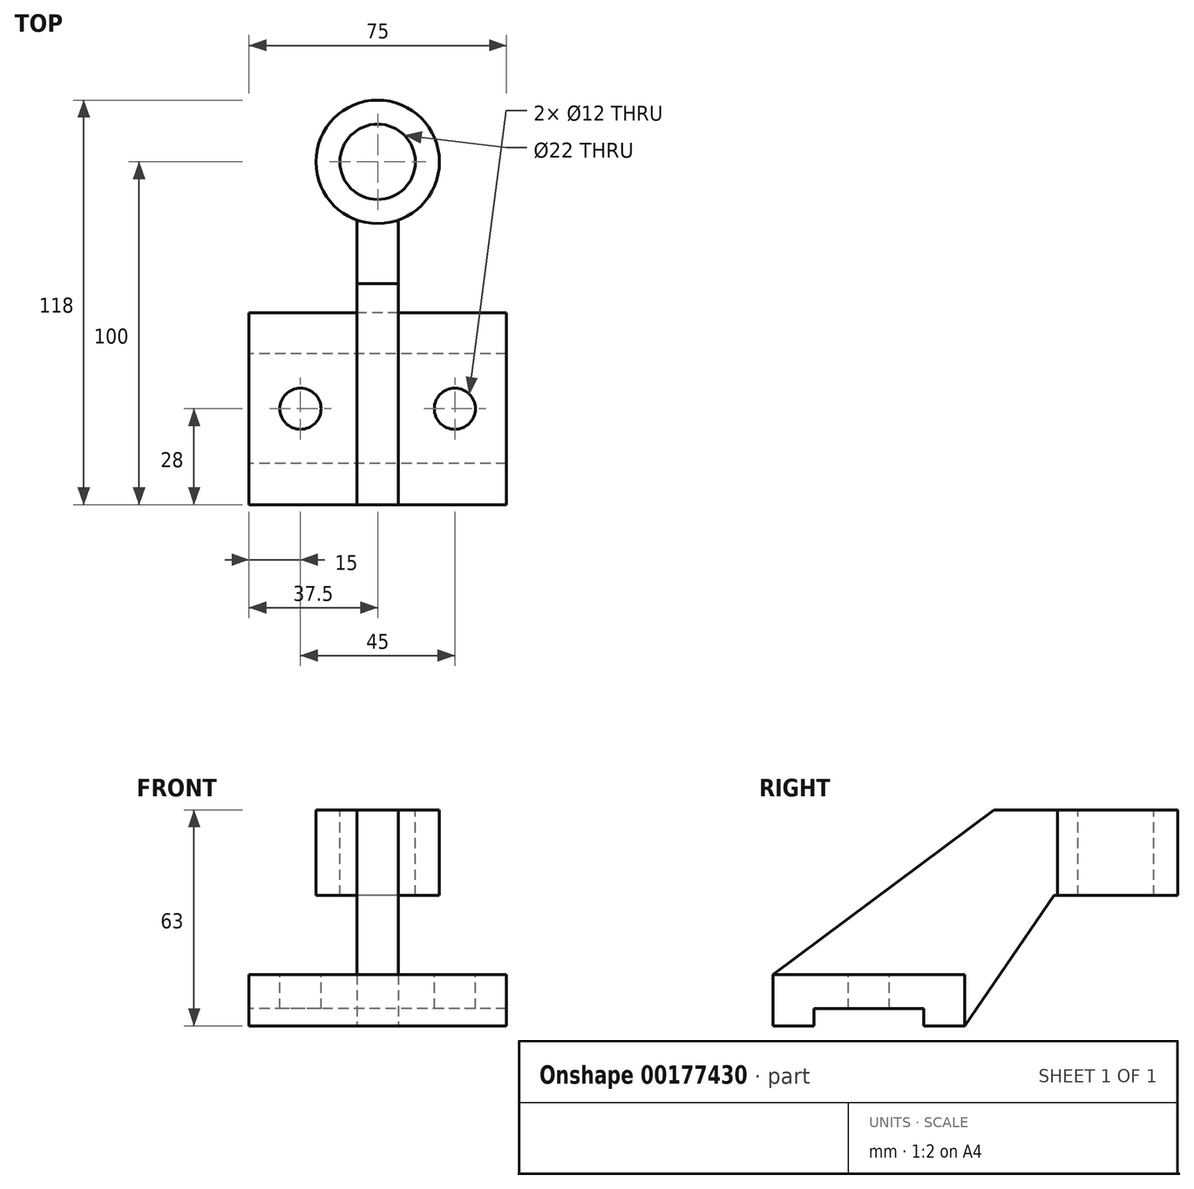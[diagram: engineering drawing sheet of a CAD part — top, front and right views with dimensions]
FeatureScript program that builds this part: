
annotation { "Feature Type Name" : "Feature", "Feature Type Description" : "" }
export const myFeature = defineFeature(function(context is Context, id is Id, definition is map)
    precondition{}
    {
        {
            var Q0;
            Q0=qCreatedBy(makeId("Right.planeOp"),FACE);
            var sketch = newSketch(context, id + "F0", { "sketchPlane" : qUnion([Q0])});
            skLineSegment(sketch, "E0", {"start": v(-28, 0) * mm, "end": v(28, 0) * mm});
            skLineSegment(sketch, "E1", {"start": v(-28, 0) * mm, "end": v(-28, -15) * mm});
            skLineSegment(sketch, "E2", {"start": v(-28, -15) * mm, "end": v(-16, -15) * mm});
            skLineSegment(sketch, "E3", {"start": v(-16, -15) * mm, "end": v(-16, -10) * mm});
            skLineSegment(sketch, "E4", {"start": v(-16, -10) * mm, "end": v(16, -10) * mm});
            skLineSegment(sketch, "E5", {"start": v(16, -10) * mm, "end": v(16, -15) * mm});
            skLineSegment(sketch, "E6", {"start": v(16, -15) * mm, "end": v(28, -15) * mm});
            skLineSegment(sketch, "E7", {"start": v(28, -15) * mm, "end": v(28, 0) * mm});
            skLineSegment(sketch, "E8", {"start": v(72, 59.68) * mm, "end": v(72, -34.73) * mm, "construction": true});
            skLineSegment(sketch, "E9", {"start": v(-23.42, 48) * mm, "end": v(96.4, 48) * mm, "construction": true});
            skLineSegment(sketch, "E10.bottom", {"start": v(54, 48) * mm, "end": v(90, 48) * mm, "construction": true});
            skLineSegment(sketch, "E10.top", {"start": v(54, 23) * mm, "end": v(90, 23) * mm, "construction": true});
            skLineSegment(sketch, "E10.left", {"start": v(54, 48) * mm, "end": v(54, 23) * mm, "construction": true});
            skLineSegment(sketch, "E10.right", {"start": v(90, 48) * mm, "end": v(90, 23) * mm, "construction": true});
            skPoint(sketch, "E11", {"position": v(72, 48) * mm});
            skLineSegment(sketch, "E12", {"start": v(36, 48) * mm, "end": v(36, 37.79) * mm, "construction": true});
            skSolve(sketch);
        }
        {
            var Q0;
            Q0 = qSketchRegion(id + "F0", true);
            extrude(context, id + "F1", {"entities" : qUnion([Q0]), "endBound" : BoundingType.SYMMETRIC, "depth" : 75 * mm});
        }
        {
            var Q0;
            Q0=makeQuery(id+"F1.opExtrude","SWEPT_FACE",FACE,{"disambiguationData":[OSD([sQuery(id+"F0.wireOp",EDGE,"E0")])]});
            var sketch = newSketch(context, id + "F2", { "sketchPlane" : qUnion([Q0])});
            skCircle(sketch, "E13", {"center": v(-22.5, 0) * mm, "radius": 6 * mm});
            skCircle(sketch, "E14.MirrorC", {"center": v(22.5, 0) * mm, "radius": 6 * mm});
            skSolve(sketch);
        }
        {
            var Q0;
            Q0 = qSketchRegion(id + "F2", true);
            extrude(context, id + "F3", {"entities" : qUnion([Q0]), "operationType" : NewBodyOperationType.REMOVE, "oppositeDirection" : true, "depth" : 25 * mm});
        }
        {
            var Q0;
            Q0=qCreatedBy(makeId("Right.planeOp"),FACE);
            var sketch = newSketch(context, id + "F4", { "sketchPlane" : qUnion([Q0])});
            skLineSegment(sketch, "E15", {"start": v(36.5, 48) * mm, "end": v(-28, 0) * mm});
            skLineSegment(sketch, "E16", {"start": v(-28, 0) * mm, "end": v(28, 0) * mm});
            skLineSegment(sketch, "E17", {"start": v(28, 0) * mm, "end": v(28, -15) * mm});
            skLineSegment(sketch, "E18", {"start": v(28, -15) * mm, "end": v(54, 23) * mm});
            skLineSegment(sketch, "E19", {"start": v(36.5, 48) * mm, "end": v(54, 48) * mm});
            skLineSegment(sketch, "E20", {"start": v(54, 23) * mm, "end": v(59, 23) * mm});
            skLineSegment(sketch, "E21", {"start": v(59, 23) * mm, "end": v(59, 47.97) * mm});
            skLineSegment(sketch, "E22", {"start": v(59, 47.97) * mm, "end": v(54, 48) * mm});
            skSolve(sketch);
        }
        {
            var Q0;
            Q0 = qSketchRegion(id + "F4", true);
            extrude(context, id + "F5", {"entities" : qUnion([Q0]), "operationType" : NewBodyOperationType.ADD, "endBound" : BoundingType.SYMMETRIC, "depth" : 12 * mm});
        }
        {
            var Q0;
            Q0=qCreatedBy(makeId("Top.planeOp"),FACE);
            cPlane(context, id + "F6", {"entities" : qUnion([Q0]), "cplaneType" : CPlaneType.OFFSET, "offset" : 48 * mm, "width" : 150 * mm, "height" : 150 * mm});
        }
        {
            var Q0;
            Q0=qCreatedBy(id+"F6.planeOp",FACE);
            var sketch = newSketch(context, id + "F7", { "sketchPlane" : qUnion([Q0])});
            skCircle(sketch, "E23", {"center": v(0, 72) * mm, "radius": 18 * mm});
            skCircle(sketch, "E24", {"center": v(0, 72) * mm, "radius": 11 * mm});
            skLineSegment(sketch, "E25", {"start": v(-6, 55.03) * mm, "end": v(6, 55.03) * mm, "construction": true});
            skSolve(sketch);
        }
        {
            var Q0;
            Q0 = qSketchRegion(id + "F7", true);
            extrude(context, id + "F8", {"entities" : qUnion([Q0]), "operationType" : NewBodyOperationType.ADD, "oppositeDirection" : true, "depth" : 25 * mm});
        }
    });
